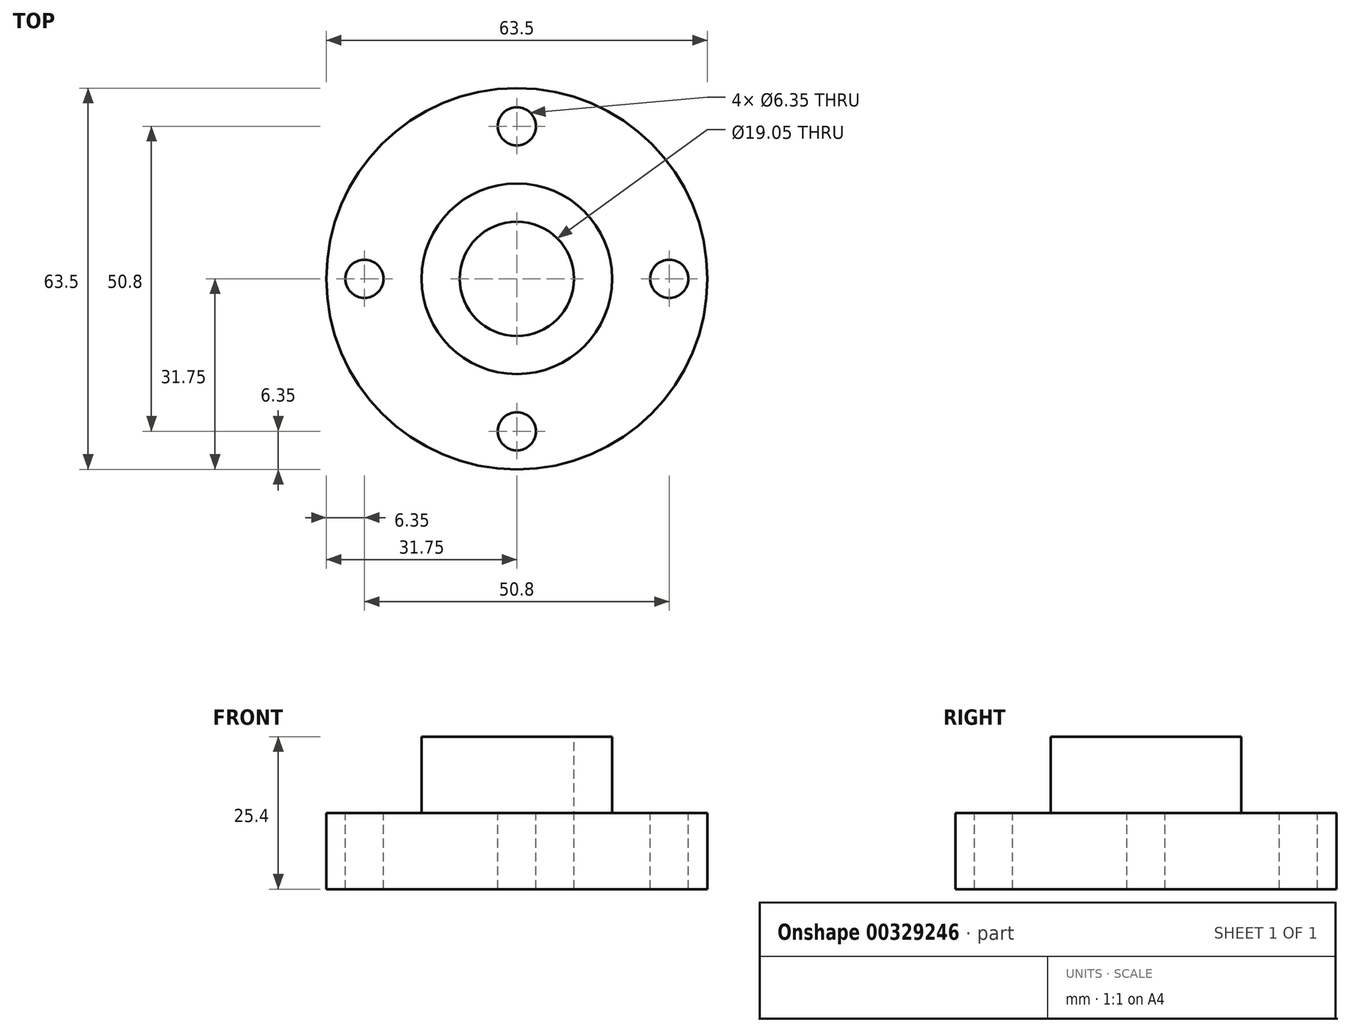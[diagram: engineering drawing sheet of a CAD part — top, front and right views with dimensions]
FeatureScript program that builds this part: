
annotation { "Feature Type Name" : "Feature", "Feature Type Description" : "" }
export const myFeature = defineFeature(function(context is Context, id is Id, definition is map)
    precondition{}
    {
        {
            var Q0;
            Q0=qCreatedBy(makeId("Top.planeOp"),FACE);
            var sketch = newSketch(context, id + "F0", { "sketchPlane" : qUnion([Q0])});
            skCircle(sketch, "E0", {"center": v(0, 0) * mm, "radius": 9.53 * mm});
            skCircle(sketch, "E1", {"center": v(0, 0) * mm, "radius": 15.88 * mm});
            skCircle(sketch, "E2", {"center": v(0, 0) * mm, "radius": 25.4 * mm});
            skCircle(sketch, "E3", {"center": v(0, 0) * mm, "radius": 31.75 * mm});
            skSolve(sketch);
        }
        {
            var Q0;
            Q0 = qSketchRegion(id + "F0", true);
            var Q1;
            Q1=makeQuery(id+"F0.imprint","IMPRINT",FACE,{"disambiguationData":[TD([[makeQuery(id+"F0.imprint","IMPRINT",EDGE,{"derivedFrom":sQuery(id+"F0.wireOp",EDGE,"E1")}),-1.0]])]});
            var Q2;
            Q2=makeQuery(id+"F0.imprint","IMPRINT",FACE,{"disambiguationData":[TD([[makeQuery(id+"F0.imprint","IMPRINT",EDGE,{"derivedFrom":sQuery(id+"F0.wireOp",EDGE,"E0")}),-1.0]])]});
            extrude(context, id + "F1", {"entities" : qUnion([Q0, Q1, Q2]), "oppositeDirection" : true, "depth" : 12.7 * mm});
        }
        {
            var Q0;
            Q0=makeQuery(id+"F0.imprint","IMPRINT",FACE,{"disambiguationData":[TD([[makeQuery(id+"F0.imprint","IMPRINT",EDGE,{"derivedFrom":sQuery(id+"F0.wireOp",EDGE,"E2")}),-1.0]])]});
            var sketch = newSketch(context, id + "F2", { "sketchPlane" : qUnion([Q0])});
            skCircle(sketch, "E4", {"center": v(0, 25.4) * mm, "radius": 3.18 * mm});
            skCircle(sketch, "E5", {"center": v(0, -25.4) * mm, "radius": 3.18 * mm});
            skCircle(sketch, "E6", {"center": v(-25.4, 0) * mm, "radius": 3.18 * mm});
            skCircle(sketch, "E7", {"center": v(25.4, 0) * mm, "radius": 3.18 * mm});
            skSolve(sketch);
        }
        {
            var Q0;
            Q0=makeQuery(id+"F0.imprint","IMPRINT",FACE,{"disambiguationData":[TD([[makeQuery(id+"F0.imprint","IMPRINT",EDGE,{"derivedFrom":sQuery(id+"F0.wireOp",EDGE,"E0")}),-1.0]])]});
            extrude(context, id + "F3", {"entities" : qUnion([Q0]), "operationType" : NewBodyOperationType.ADD, "depth" : 12.7 * mm});
        }
        {
            var Q0;
            Q0 = qSketchRegion(id + "F2", true);
            extrude(context, id + "F4", {"entities" : qUnion([Q0]), "operationType" : NewBodyOperationType.REMOVE, "endBound" : BoundingType.THROUGH_ALL, "oppositeDirection" : true, "depth" : 25.4 * mm});
        }
    });
